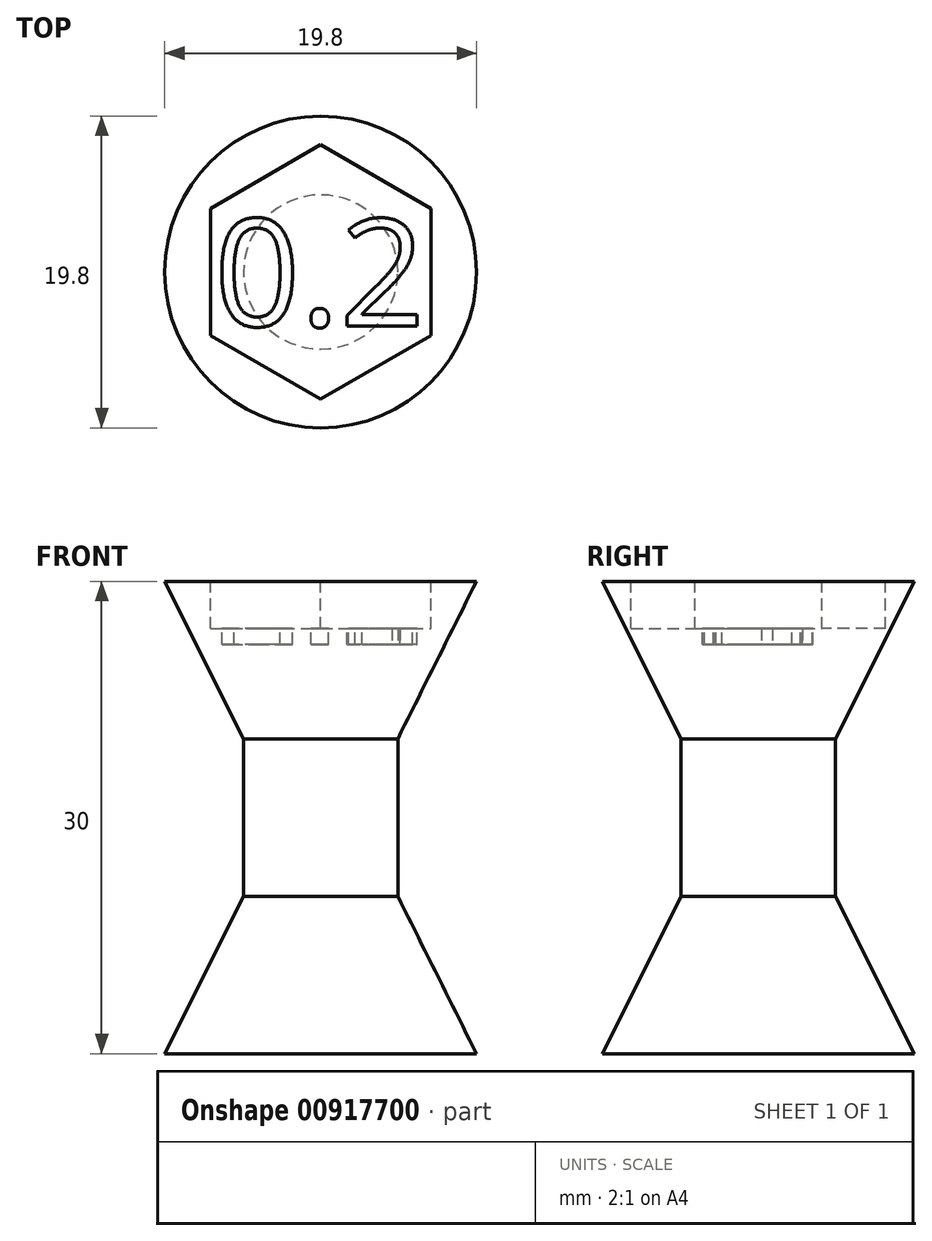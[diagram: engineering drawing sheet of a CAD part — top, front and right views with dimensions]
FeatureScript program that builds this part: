
annotation { "Feature Type Name" : "Feature", "Feature Type Description" : "" }
export const myFeature = defineFeature(function(context is Context, id is Id, definition is map)
    precondition{}
    {
        {
            var Q0;
            Q0=qCreatedBy(makeId("Front.planeOp"),FACE);
            var sketch = newSketch(context, id + "F0", { "sketchPlane" : qUnion([Q0])});
            skLineSegment(sketch, "E0", {"start": v(0, 15) * mm, "end": v(0, -15) * mm});
            skLineSegment(sketch, "E1", {"start": v(0, -15) * mm, "end": v(9.9, -15) * mm});
            skLineSegment(sketch, "E2", {"start": v(9.9, -15) * mm, "end": v(4.9, -5) * mm});
            skLineSegment(sketch, "E3", {"start": v(4.9, -5) * mm, "end": v(4.9, 5) * mm});
            skLineSegment(sketch, "E4", {"start": v(4.9, 5) * mm, "end": v(9.9, 15) * mm});
            skLineSegment(sketch, "E5", {"start": v(9.9, 15) * mm, "end": v(0, 15) * mm});
            skSolve(sketch);
        }
        {
            var Q0;
            Q0 = qSketchRegion(id + "F0", true);
            var Q1;
            Q1=sQuery(id+"F0.wireOp",EDGE,"E0");
            revolve(context, id + "F1", {"surfaceOperationType" : NewSurfaceOperationType.NEW, "entities" : qUnion([Q0]), "axis" : qUnion([Q1]), "revolveType" : RevolveType.FULL});
        }
        {
            var Q0;
            Q0=makeQuery(id+"F1.opRevolve","SWEPT_FACE",FACE,{"disambiguationData":[OSD([sQuery(id+"F0.wireOp",EDGE,"E5")])]});
            var sketch = newSketch(context, id + "F2", { "sketchPlane" : qUnion([Q0])});
            skCircle(sketch, "E6.cCircle", {"center": v(0, 0) * mm, "radius": 7 * mm, "construction": true});
            skLineSegment(sketch, "E6.0", {"start": v(0, 8.08) * mm, "end": v(7, 4.04) * mm});
            skLineSegment(sketch, "E6.1", {"start": v(7, 4.04) * mm, "end": v(7, -4.04) * mm});
            skLineSegment(sketch, "E6.2", {"start": v(7, -4.04) * mm, "end": v(0, -8.08) * mm});
            skLineSegment(sketch, "E6.3", {"start": v(0, -8.08) * mm, "end": v(-7, -4.04) * mm});
            skLineSegment(sketch, "E6.4", {"start": v(-7, -4.04) * mm, "end": v(-7, 4.04) * mm});
            skLineSegment(sketch, "E6.5", {"start": v(-7, 4.04) * mm, "end": v(0, 8.08) * mm});
            skPoint(sketch, "E6.0.midPoint", {"position": v(3.5, 6.06) * mm});
            skSolve(sketch);
        }
        {
            var Q0;
            Q0 = qSketchRegion(id + "F2", true);
            extrude(context, id + "F3", {"entities" : qUnion([Q0]), "operationType" : NewBodyOperationType.REMOVE, "oppositeDirection" : true, "depth" : 3 * mm, "offsetDistance" : 25 * mm});
        }
        {
            var Q0;
            Q0=makeQuery(id+"F3.boolean.opBoolean","COPY",FACE,{"derivedFrom":makeQuery(id+"F3.opExtrude","CAP_FACE",FACE,{"disambiguationData":[OSD([sQuery(id+"F2.wireOp",EDGE,"E6.0"),sQuery(id+"F2.wireOp",EDGE,"E6.1"),sQuery(id+"F2.wireOp",EDGE,"E6.2"),sQuery(id+"F2.wireOp",EDGE,"E6.3"),sQuery(id+"F2.wireOp",EDGE,"E6.4"),sQuery(id+"F2.wireOp",EDGE,"E6.5")])],"isStart":false})});
            var sketch = newSketch(context, id + "F4", { "sketchPlane" : qUnion([Q0])});
            skText(sketch, "E7", { "text": "0.2", "fontName": "OpenSans-Regular.ttf"});
            const initialGuessF4  = {"E7": [-0.00675, -0.00343, 1, 0, 0.00684]};
            skSetInitialGuess(sketch, initialGuessF4);
            skSolve(sketch);
        }
        {
            var Q0;
            Q0 = qSketchRegion(id + "F4", true);
            extrude(context, id + "F5", {"entities" : qUnion([Q0]), "operationType" : NewBodyOperationType.REMOVE, "oppositeDirection" : true, "depth" : 1 * mm, "offsetDistance" : 25 * mm});
        }
    });
